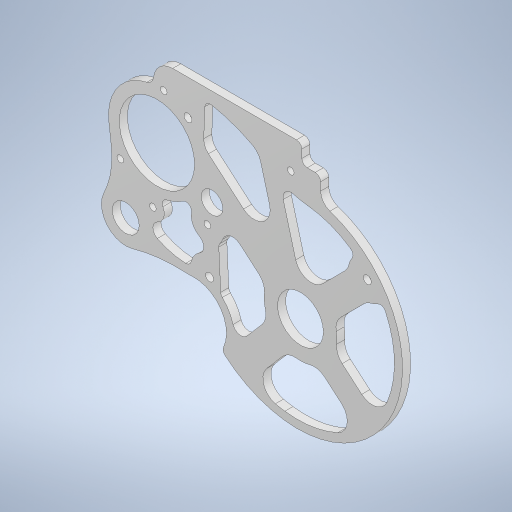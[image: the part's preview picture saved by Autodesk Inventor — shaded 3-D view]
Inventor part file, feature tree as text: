
AUTODESK INVENTOR PART (.ipt)
format: ipt  version: 2023.1 (Build 271208000, 208)  size: 521,728 bytes
history: native  units: mm
features: other x4, sketch x1
ambient origin geometry x8: Origin, YZ Plane, XZ Plane, XY Plane, X Axis, Y Axis, Z Axis, Center Point
bodies: Solid3 (feature_tree)
feature tree (5):
  other  "足内フレーム.ipt"
  other  "Solid3::足内フレーム.ipt"
  other  "TaggingFeature1"
  sketch  "Sketch9"  dims[d0=10.0mm]
  other  "sesaku"
